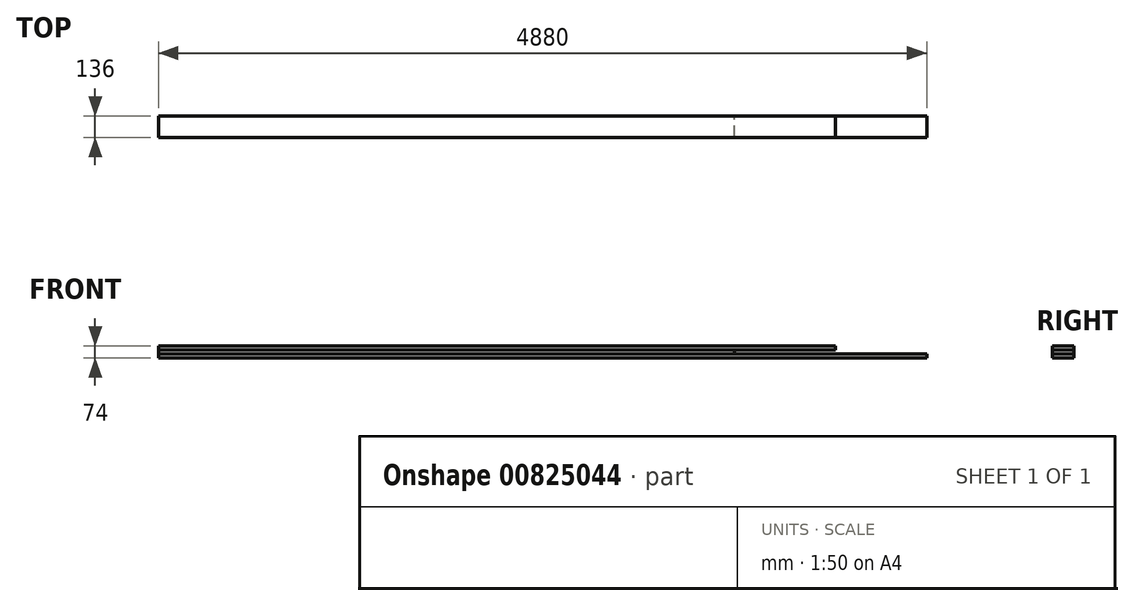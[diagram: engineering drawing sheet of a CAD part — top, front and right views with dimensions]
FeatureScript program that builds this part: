
annotation { "Feature Type Name" : "Feature", "Feature Type Description" : "" }
export const myFeature = defineFeature(function(context is Context, id is Id, definition is map)
    precondition{}
    {
        {
            var Q0;
            Q0=qCreatedBy(makeId("Right.planeOp"),FACE);
            var sketch = newSketch(context, id + "F0", { "sketchPlane" : qUnion([Q0])});
            skLineSegment(sketch, "E0.bottom", {"start": v(-136, 0) * mm, "end": v(0, 0) * mm});
            skLineSegment(sketch, "E0.top", {"start": v(-136, 24) * mm, "end": v(0, 24) * mm});
            skLineSegment(sketch, "E0.left", {"start": v(-136, 0) * mm, "end": v(-136, 24) * mm});
            skLineSegment(sketch, "E0.right", {"start": v(0, 0) * mm, "end": v(0, 24) * mm});
            skLineSegment(sketch, "E1.0.1.0", {"start": v(0, 25) * mm, "end": v(0, 49) * mm});
            skLineSegment(sketch, "E1.0.1.1", {"start": v(-136, 49) * mm, "end": v(0, 49) * mm});
            skLineSegment(sketch, "E1.0.1.2", {"start": v(-136, 25) * mm, "end": v(-136, 49) * mm});
            skLineSegment(sketch, "E1.0.1.3", {"start": v(-136, 25) * mm, "end": v(0, 25) * mm});
            skLineSegment(sketch, "E1.0.2.0", {"start": v(0, 50) * mm, "end": v(0, 74) * mm});
            skLineSegment(sketch, "E1.0.2.1", {"start": v(-136, 74) * mm, "end": v(0, 74) * mm});
            skLineSegment(sketch, "E1.0.2.2", {"start": v(-136, 50) * mm, "end": v(-136, 74) * mm});
            skLineSegment(sketch, "E1.0.2.3", {"start": v(-136, 50) * mm, "end": v(0, 50) * mm});
            skLineSegment(sketch, "E1.direction1", {"start": v(0, 24) * mm, "end": v(25, 24) * mm, "construction": true});
            skLineSegment(sketch, "E1.direction2", {"start": v(0, 24) * mm, "end": v(0, 49) * mm, "construction": true});
            skSolve(sketch);
        }
        {
            var Q0;
            Q0=makeQuery(id+"F0.imprint","IMPRINT",FACE,{"disambiguationData":[TD([[makeQuery(id+"F0.imprint","IMPRINT",EDGE,{"derivedFrom":sQuery(id+"F0.wireOp",EDGE,"E0.bottom")}),1.0]])]});
            extrude(context, id + "F1", {"entities" : qUnion([Q0]), "depth" : 4880 * mm, "offsetDistance" : 25 * mm});
        }
        {
            var Q0;
            Q0=makeQuery(id+"F0.imprint","IMPRINT",FACE,{"disambiguationData":[TD([[makeQuery(id+"F0.imprint","IMPRINT",EDGE,{"derivedFrom":sQuery(id+"F0.wireOp",EDGE,"E1.0.1.0")}),1.0]])]});
            extrude(context, id + "F2", {"entities" : qUnion([Q0]), "depth" : 3660 * mm, "offsetDistance" : 25 * mm});
        }
        {
            var Q0;
            Q0=makeQuery(id+"F0.imprint","IMPRINT",FACE,{"disambiguationData":[TD([[makeQuery(id+"F0.imprint","IMPRINT",EDGE,{"derivedFrom":sQuery(id+"F0.wireOp",EDGE,"E1.0.2.0")}),1.0]])]});
            extrude(context, id + "F3", {"entities" : qUnion([Q0]), "depth" : 4300 * mm, "offsetDistance" : 25 * mm});
        }
    });
